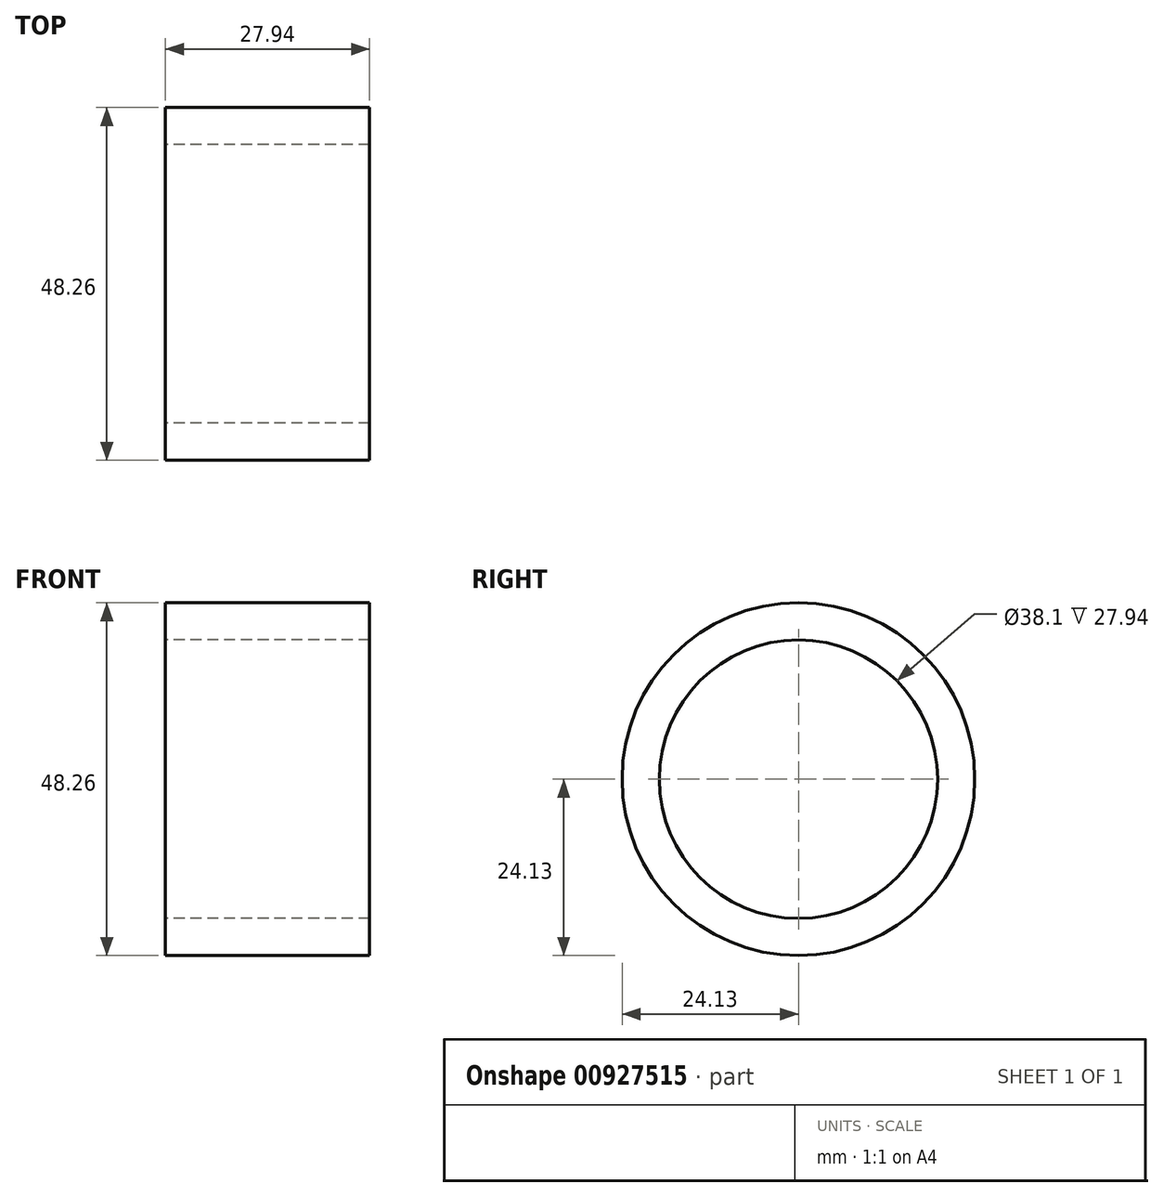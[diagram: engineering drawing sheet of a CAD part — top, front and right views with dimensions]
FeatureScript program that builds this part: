
annotation { "Feature Type Name" : "Feature", "Feature Type Description" : "" }
export const myFeature = defineFeature(function(context is Context, id is Id, definition is map)
    precondition{}
    {
        {
            var Q0;
            Q0=qCreatedBy(makeId("Right.planeOp"),FACE);
            var sketch = newSketch(context, id + "F0", { "sketchPlane" : qUnion([Q0])});
            skCircle(sketch, "E0", {"center": v(0, 0) * mm, "radius": 24.13 * mm});
            skCircle(sketch, "E1", {"center": v(0, 0) * mm, "radius": 19.05 * mm});
            skSolve(sketch);
        }
        {
            var Q0;
            Q0=makeQuery(id+"F0.imprint","IMPRINT",FACE,{"disambiguationData":[TD([[makeQuery(id+"F0.imprint","IMPRINT",EDGE,{"derivedFrom":sQuery(id+"F0.wireOp",EDGE,"E0")}),1.0]])]});
            extrude(context, id + "F1", {"entities" : qUnion([Q0]), "depth" : 27.94 * mm, "offsetDistance" : 25.4 * mm});
        }
    });
